# Revit family: Сливной KFE-кран SX 10638
name_source: partatom
category: Арматура трубопроводов
revit_build: Autodesk Revit 2017 (Build: 20171027_0315(x64)
units: mm (PartAtom-declared; Revit-internal decimal feet)

## family parameters
Всегда вертикально = Да
На основе рабочей плоскости = Нет
Общий = Нет
При загрузке вырезать с полостями = Нет
Размер круглого соединителя = Использовать радиус
Тип детали = Вставляется

## types (1)
- Сливной KFE-кран SX 10638
    ADSK_Единица измерения = шт
    ADSK_Завод-изготовитель = Itap
    ADSK_Код изделия = SX 10638
    ADSK_Масса = 0
    ADSK_Наименование = Кран шоровой латунный KFE Exclusive HP, PN16bar, прямой, со штуцером
    ADSK_Обозначение = DN15
    C = 47 мм
    C1 = 20 мм
    D = 40 мм
    D2 = 13 мм
    DN = 15 мм
    DN2 = 20 мм
    E = 11 мм
    F = 28 мм
    G = 15 мм
    R1 = 8 мм
    R2 = 10 мм
    URL = http://www.meibes.ru
    s = 24 мм
    t = 2 мм
    Группа модели = Кран шоровой латунный KFE Exclusive HP, PN16bar, прямой, со штуцером
    Изготовитель = Itap
    Материал полимера = Фильтр_Черный
    Материал стальной части = Сталь
    Материал фитинга = РВК_Полипропилен PPR
    Переключатель УГО = Да
    Разработчик = ООО ПРОРУБИМ
    Разработчик (телефон) = +7(495)649-85-43
    Разработчик модели (URL) = http://prorubim.com
